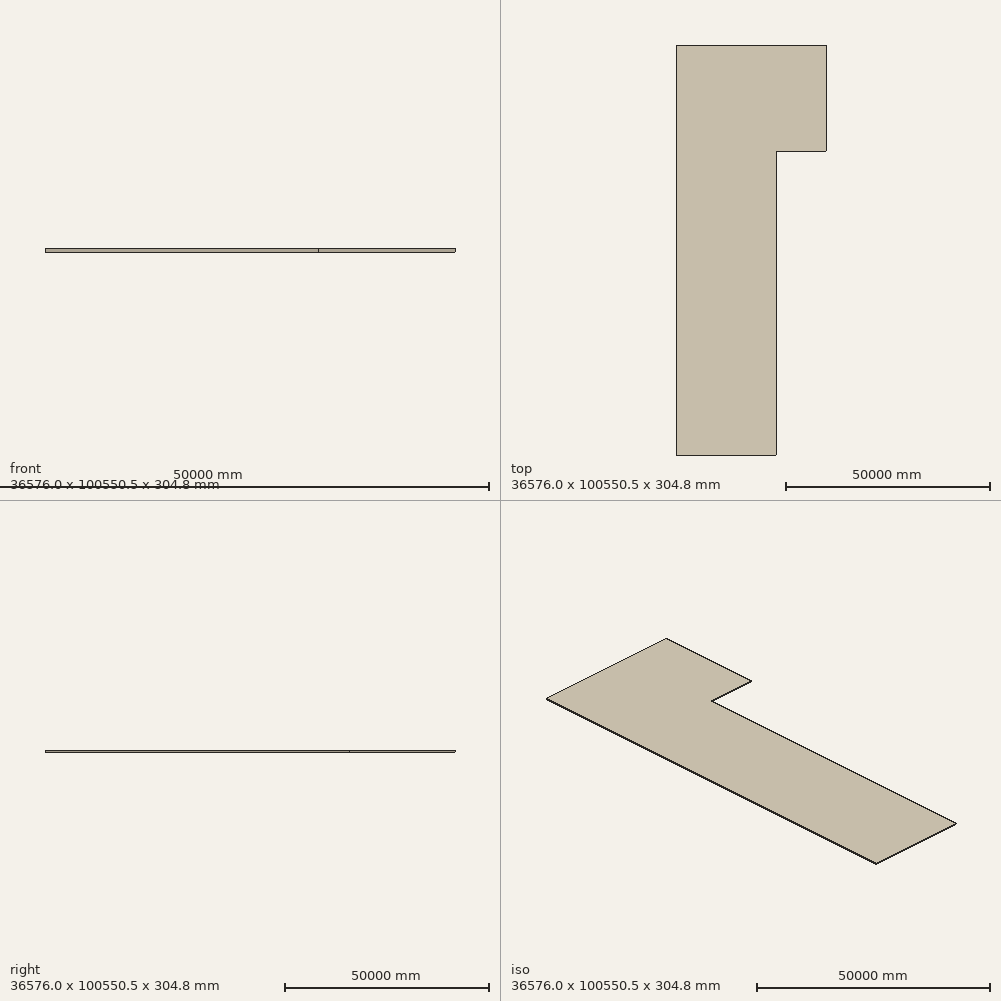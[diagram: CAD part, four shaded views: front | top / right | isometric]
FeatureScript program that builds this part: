
annotation { "Feature Type Name" : "Feature", "Feature Type Description" : "" }
export const myFeature = defineFeature(function(context is Context, id is Id, definition is map)
    precondition{}
    {
        {
            var Q0;
            Q0=qCreatedBy(makeId("Top.planeOp"),FACE);
            var sketch = newSketch(context, id + "F0", { "sketchPlane" : qUnion([Q0])});
            skLineSegment(sketch, "E0.bottom", {"start": v(0, 0) * mm, "end": v(24384, 0) * mm});
            skLineSegment(sketch, "E0.top", {"start": v(0, 100550.47) * mm, "end": v(36576, 100550.47) * mm});
            skLineSegment(sketch, "E0.left", {"start": v(0, 0) * mm, "end": v(0, 100550.47) * mm});
            skLineSegment(sketch, "E0.right", {"start": v(24384, 0) * mm, "end": v(24384, 74624.18) * mm});
            skLineSegment(sketch, "E1", {"start": v(24384, 74624.18) * mm, "end": v(36576, 74624.18) * mm});
            skLineSegment(sketch, "E2", {"start": v(36576, 74624.18) * mm, "end": v(36576, 100550.47) * mm});
            skSolve(sketch);
        }
        {
            var Q0;
            Q0 = qSketchRegion(id + "F0", true);
            extrude(context, id + "F1", {"entities" : qUnion([Q0]), "depth" : 304.8 * mm, "offsetDistance" : 25.4 * mm});
        }
    });
